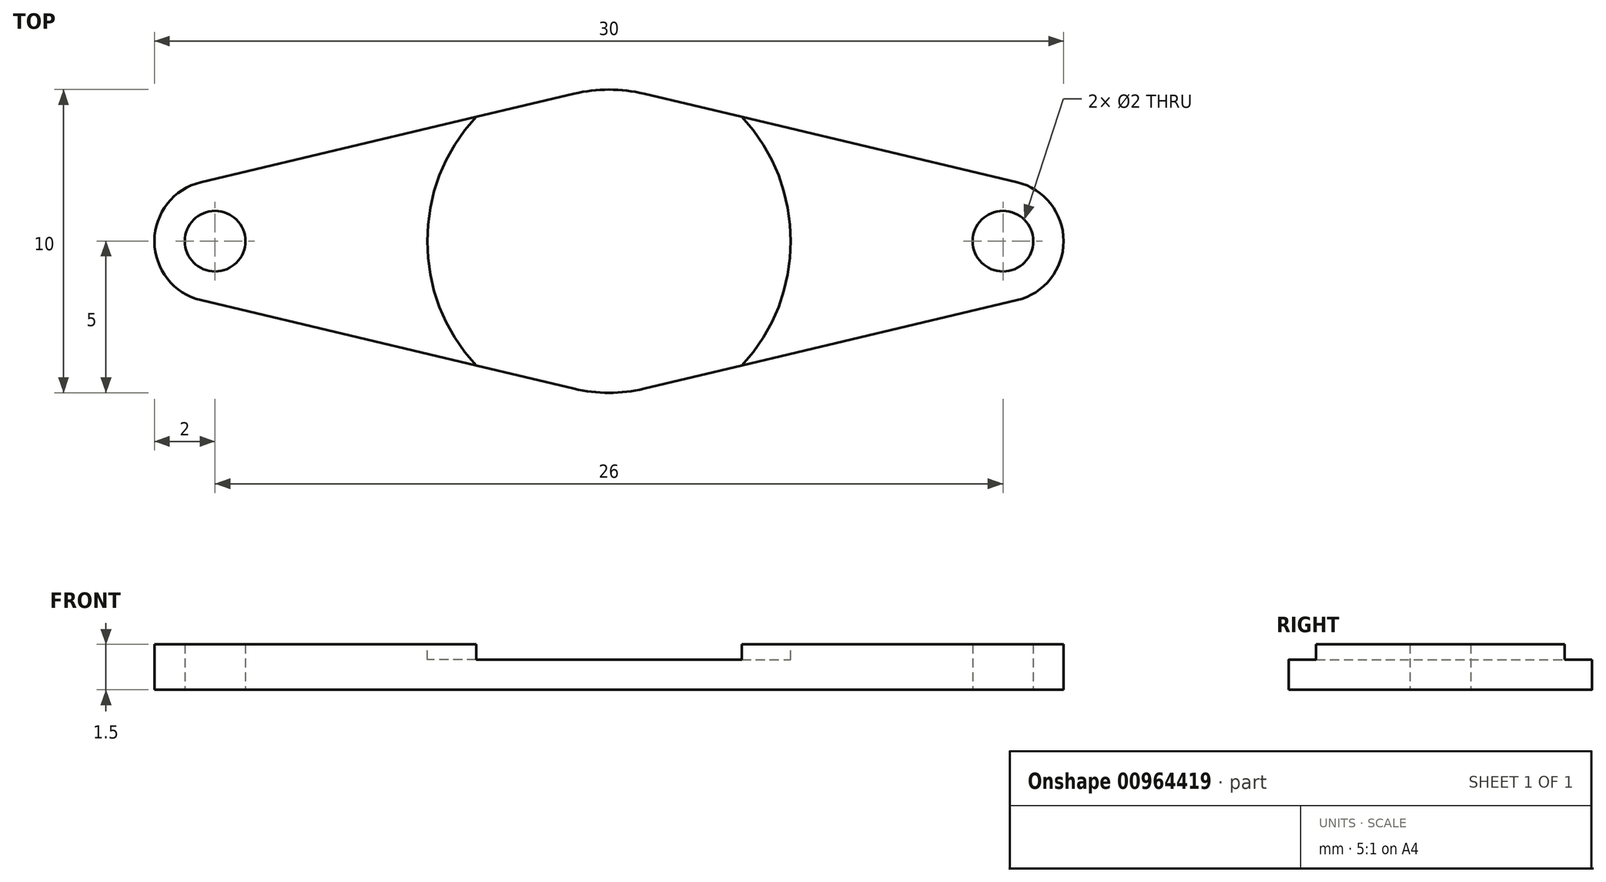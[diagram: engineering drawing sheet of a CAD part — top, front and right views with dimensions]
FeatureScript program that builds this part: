
annotation { "Feature Type Name" : "Feature", "Feature Type Description" : "" }
export const myFeature = defineFeature(function(context is Context, id is Id, definition is map)
    precondition{}
    {
        {
            var Q0;
            Q0=qCreatedBy(makeId("Top.planeOp"),FACE);
            var sketch = newSketch(context, id + "F0", { "sketchPlane" : qUnion([Q0])});
            skArc(sketch, "E0", {"start": v(1.15, 4.87) * mm, "mid": v(0, 5) * mm, "end": v(-1.15, 4.87) * mm});
            skArc(sketch, "E1", {"start": v(-13.46, 1.95) * mm, "mid": v(-15, 0) * mm, "end": v(-13.46, -1.95) * mm});
            skLineSegment(sketch, "E2", {"start": v(-13.46, -1.95) * mm, "end": v(-1.15, -4.87) * mm});
            skLineSegment(sketch, "E3", {"start": v(-1.15, 4.87) * mm, "end": v(-13.46, 1.95) * mm});
            skLineSegment(sketch, "E4.MirrorCS", {"start": v(13.46, -1.95) * mm, "end": v(1.15, -4.87) * mm});
            skLineSegment(sketch, "E5.MirrorCS", {"start": v(1.15, 4.87) * mm, "end": v(13.46, 1.95) * mm});
            skArc(sketch, "E6.MirrorCS", {"start": v(13.46, 1.95) * mm, "mid": v(15, 0) * mm, "end": v(13.46, -1.95) * mm});
            skArc(sketch, "E7.trimOffspring", {"start": v(-1.15, -4.87) * mm, "mid": v(0, -5) * mm, "end": v(1.15, -4.87) * mm});
            skCircle(sketch, "E8", {"center": v(-13, 0) * mm, "radius": 1 * mm});
            skCircle(sketch, "E9.MirrorC", {"center": v(13, 0) * mm, "radius": 1 * mm});
            skSolve(sketch);
        }
        {
            var Q0;
            Q0 = qSketchRegion(id + "F0", true);
            extrude(context, id + "F1", {"entities" : qUnion([Q0]), "depth" : 1.5 * mm, "offsetDistance" : 25 * mm});
        }
        {
            var Q0;
            Q0=makeQuery(id+"F1.opExtrude","CAP_FACE",FACE,{"disambiguationData":[OSD([sQuery(id+"F0.wireOp",EDGE,"E0"),sQuery(id+"F0.wireOp",EDGE,"E1"),sQuery(id+"F0.wireOp",EDGE,"E2"),sQuery(id+"F0.wireOp",EDGE,"E3"),sQuery(id+"F0.wireOp",EDGE,"E4.MirrorCS"),sQuery(id+"F0.wireOp",EDGE,"E5.MirrorCS"),sQuery(id+"F0.wireOp",EDGE,"E6.MirrorCS"),sQuery(id+"F0.wireOp",EDGE,"E7.trimOffspring"),sQuery(id+"F0.wireOp",EDGE,"E8"),sQuery(id+"F0.wireOp",EDGE,"cmW3fhEA-egvJ-hO24-3JMP-FZg6UGn3whrK")])],"isStart":false});
            var sketch = newSketch(context, id + "F2", { "sketchPlane" : qUnion([Q0])});
            skCircle(sketch, "E10", {"center": v(0, 0) * mm, "radius": 6 * mm});
            skSolve(sketch);
        }
        {
            var Q0;
            Q0=makeQuery(id+"F2.imprint","IMPRINT",FACE,{"disambiguationData":[TD([[makeQuery(id+"F2.imprint","IMPRINT",EDGE,{"derivedFrom":sQuery(id+"F2.wireOp",EDGE,"E10")}),1.0]])]});
            extrude(context, id + "F3", {"entities" : qUnion([Q0]), "operationType" : NewBodyOperationType.REMOVE, "oppositeDirection" : true, "depth" : .5 * mm, "offsetDistance" : 25 * mm});
        }
    });
